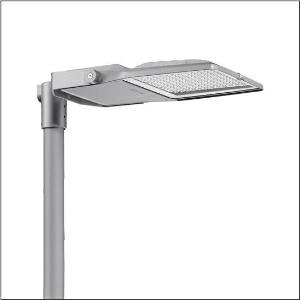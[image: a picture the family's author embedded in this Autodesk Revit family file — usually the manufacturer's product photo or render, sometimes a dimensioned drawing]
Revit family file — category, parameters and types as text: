
# Revit family: floodlight_fl_21_iq_midi___pl33t_5xa7781e4f3a_bb4e
name_source: partatom
category: Lighting Fixtures
units: mm (PartAtom-declared; Revit-internal decimal feet)

## family parameters
Cut with Voids When Loaded = No
Host = Face
Light Source = No
Part Type = Normal
Room Calculation Point = No
Round Connector Dimension = Use Diameter
Shared = No

## types (1)
- --- (1 x LED, 27690 lm, 208.1 W, 4000K)
    Apparent Load = 208 VA
    CIE Flux Codes = 26 75 99 100 100
    Color Rendering = 70
    Color Temperature = 4000K
    Default Elevation = 1800 mm
    Description = Floodlight FL 21 iQ midi, floodlight, primary light control with lens, of PMMA, primary optical cover: protective disc, of toughened safety glass, transparent, light distribution: PL33T, light emission: direct distribution, installation type: surface-mounted, LED, High Power LED, rated luminous flux: 27.690lm, luminous efficacy: 133lm/W, light colour: 740, colour temperature: 4000K, control gear: ECG iQ, control: optimised constant luminous flux control (CLO 2.0), Desk-Remote (wireless, voltage-free reading and setting of iQ features in the workshop via application-optimized NFC function/RFID function), Light-Fading, Smart-Wire, Night-Set, Lumen-Switch, Temp-Guard, Auto-Match, with terminal, 6-pole, mains connection: 220..240V, AC, 50/60Hz, start of lifetime: 208W, end of service life: 227W, reduction: 90W, luminaire housing, of diecast aluminium, powder-coated, Siteco® metallic grey (DB 702S), corrosivity category C5 mid according to DIN EN ISO 12944, sealing non-destructively replaceable, please order mast flange separately, mast bracket, of steel, galvanised, powder-coated, Siteco® metallic grey (DB 702S), protection rating (complete): IP66, insulation class (complete): insulation class II (safety insulation), certification: CE, protection symbol: D, impact resistance: IK08, permissible operating ambient temperature: -40..+40°C, permissible operating ambient temperature for outdoor applications: -40..+50°C, standard: DIN EN 12944, LABS conformity tested according to VDMA 24364:2018-05, packaging unit: 1 piece

Light Distribution: PL33T
    Height = 76 mm
    Lamp = 1 x LED
    Lamp Light Flux = 27690 lm
    Lamp Power = 208.1 W
    Lamp count = 1
    Length = 657 mm
    Luminous efficacy = 133 lm/W
    Manufacturer = Siteco
    ModVariant = No
    Model = 5XA7781E4F3A
    Number of Poles = 1
    OnlyDefault = Yes
    Power Factor = 1
    Product Name = Floodlight FL 21 iQ midi | PL33T
    Product group = floodlight | pylon annexe
    ProductGroupID = 6200
    Protection Class = Protection class II
    Protection Degree = IP 66
    RLX_Detail_Level = 1
    RLX_Emergency_Light_Flux = 0 lm
    RLX_Emergency_Type = 0
    RLX_Emergency_Type_DB = No
    RlxData = <blob elided: 153521 chars, md5=ded7783c>
    Socket = socket
    Standby Power = 0 W
    System Light Flux = 27690 lm
    System Power = 208 W
    Type Comments = factory setting: luminous flux: 100 % | dim-lin: 254 | 710 mA
    Type Image = l_1007123.jpg
    URL = http://relux.com
    VarID = @adj_034071
    Voltage = 0 V
    Weight = 0.00 kg
    Width = 442 mm

## geometry (parser evidence)
native form markers: Blend x4, Sweep x12
no freeform markers — native parametric forms only
